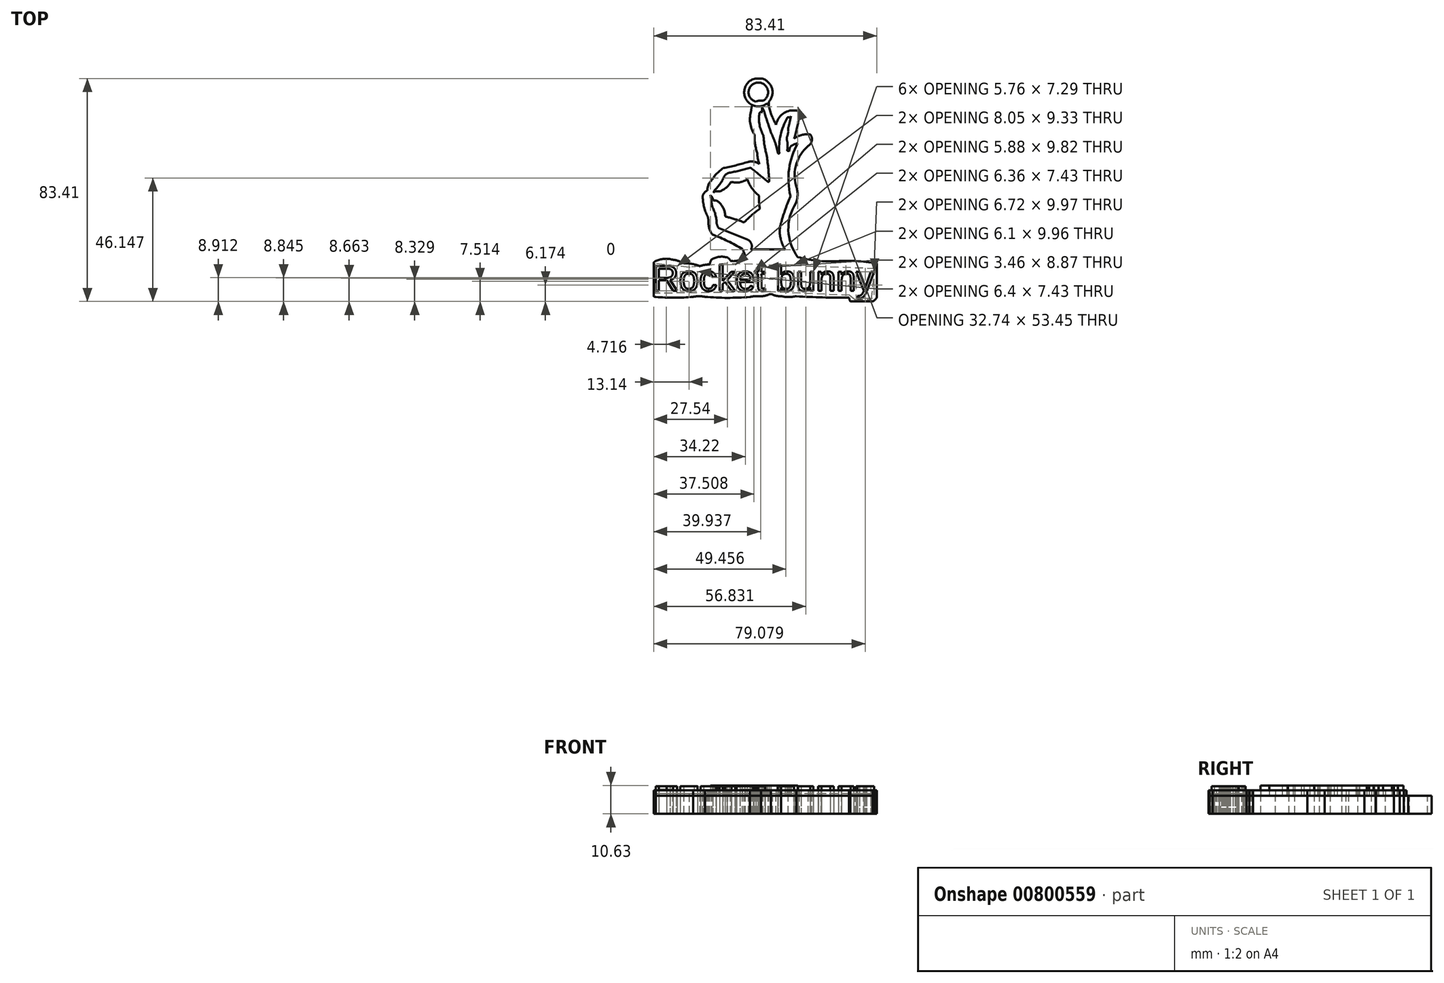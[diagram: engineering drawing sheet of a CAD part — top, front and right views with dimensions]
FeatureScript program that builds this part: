
annotation { "Feature Type Name" : "Feature", "Feature Type Description" : "" }
export const myFeature = defineFeature(function(context is Context, id is Id, definition is map)
    precondition{}
    {
        {
            var Q0;
            Q0=qCreatedBy(makeId("Top.planeOp"),FACE);
            var sketch = newSketch(context, id + "F0", { "sketchPlane" : qUnion([Q0])});
            skText(sketch, "E0", { "text": "Rocket bunny", "fontName": "Arimo-Regular.ttf"});
            skLineSegment(sketch, "E1.bottom", {"start": v(-48.47, 33.5) * mm, "end": v(34.94, 33.5) * mm});
            skLineSegment(sketch, "E1.top", {"start": v(-48.47, -49.92) * mm, "end": v(34.94, -49.92) * mm});
            skLineSegment(sketch, "E1.left", {"start": v(-48.47, 33.5) * mm, "end": v(-48.47, -49.92) * mm});
            skLineSegment(sketch, "E1.right", {"start": v(34.94, 33.5) * mm, "end": v(34.94, -49.92) * mm});
            const initialGuessF0  = {"E0": [-0.04889, -0.04592, 1, 0, 0.00976]};
            skSetInitialGuess(sketch, initialGuessF0);
            skSolve(sketch);
        }
        {
            var Q0;
            Q0=makeQuery(id+"F0.imprint","IMPRINT",FACE,{"disambiguationData":[TD([[makeQuery(id+"F0.imprint","IMPRINT",EDGE,{"derivedFrom":sQuery(id+"F0.wireOp",EDGE,"E0.sketch_text.stroke-0")}),-1.0]])]});
            var Q1;
            Q1=makeQuery(id+"F0.imprint","IMPRINT",FACE,{"disambiguationData":[TD([[makeQuery(id+"F0.imprint","IMPRINT",EDGE,{"derivedFrom":sQuery(id+"F0.wireOp",EDGE,"E0.sketch_text.stroke-19")}),-1.0]])]});
            var Q2;
            Q2=makeQuery(id+"F0.imprint","IMPRINT",FACE,{"disambiguationData":[TD([[makeQuery(id+"F0.imprint","IMPRINT",EDGE,{"derivedFrom":sQuery(id+"F0.wireOp",EDGE,"E0.sketch_text.stroke-34")}),-1.0]])]});
            var Q3;
            Q3=makeQuery(id+"F0.imprint","IMPRINT",FACE,{"disambiguationData":[TD([[makeQuery(id+"F0.imprint","IMPRINT",EDGE,{"derivedFrom":sQuery(id+"F0.wireOp",EDGE,"E0.sketch_text.stroke-52")}),-1.0]])]});
            var Q4;
            Q4=makeQuery(id+"F0.imprint","IMPRINT",FACE,{"disambiguationData":[TD([[makeQuery(id+"F0.imprint","IMPRINT",EDGE,{"derivedFrom":sQuery(id+"F0.wireOp",EDGE,"E0.sketch_text.stroke-64")}),-1.0]])]});
            var Q5;
            Q5=makeQuery(id+"F0.imprint","IMPRINT",FACE,{"disambiguationData":[TD([[makeQuery(id+"F0.imprint","IMPRINT",EDGE,{"derivedFrom":sQuery(id+"F0.wireOp",EDGE,"E0.sketch_text.stroke-82")}),-1.0]])]});
            var Q6;
            Q6=makeQuery(id+"F0.imprint","IMPRINT",FACE,{"disambiguationData":[TD([[makeQuery(id+"F0.imprint","IMPRINT",EDGE,{"derivedFrom":sQuery(id+"F0.wireOp",EDGE,"E0.sketch_text.stroke-99")}),-1.0]])]});
            var Q7;
            Q7=makeQuery(id+"F0.imprint","IMPRINT",FACE,{"disambiguationData":[TD([[makeQuery(id+"F0.imprint","IMPRINT",EDGE,{"derivedFrom":sQuery(id+"F0.wireOp",EDGE,"E0.sketch_text.stroke-124")}),-1.0]])]});
            var Q8;
            Q8=makeQuery(id+"F0.imprint","IMPRINT",FACE,{"disambiguationData":[TD([[makeQuery(id+"F0.imprint","IMPRINT",EDGE,{"derivedFrom":sQuery(id+"F0.wireOp",EDGE,"E0.sketch_text.stroke-145")}),-1.0]])]});
            var Q9;
            Q9=makeQuery(id+"F0.imprint","IMPRINT",FACE,{"disambiguationData":[TD([[makeQuery(id+"F0.imprint","IMPRINT",EDGE,{"derivedFrom":sQuery(id+"F0.wireOp",EDGE,"E0.sketch_text.stroke-166")}),-1.0]])]});
            var Q10;
            Q10=makeQuery(id+"F0.imprint","IMPRINT",FACE,{"disambiguationData":[TD([[makeQuery(id+"F0.imprint","IMPRINT",EDGE,{"derivedFrom":sQuery(id+"F0.wireOp",EDGE,"E0.sketch_text.stroke-187")}),-1.0]])]});
            extrude(context, id + "F1", {"entities" : qUnion([Q0, Q1, Q2, Q3, Q4, Q5, Q6, Q7, Q8, Q9, Q10]), "depth" : 25.4 * mm, "offsetDistance" : 25.4 * mm});
        }
        {
            var Q0;
            Q0 = qSketchRegion(id + "F0", true);
            extrude(context, id + "F2", {"entities" : qUnion([Q0]), "depth" : 21.84 * mm, "offsetDistance" : 25.4 * mm});
        }
        {
            var Q0;
            Q0=makeQuery(id+"F2.opExtrude","CAP_FACE",FACE,{"disambiguationData":[OSD([sQuery(id+"F0.wireOp",EDGE,"E0.sketch_text.stroke-0"),sQuery(id+"F0.wireOp",EDGE,"E0.sketch_text.stroke-1"),sQuery(id+"F0.wireOp",EDGE,"E0.sketch_text.stroke-2"),sQuery(id+"F0.wireOp",EDGE,"E0.sketch_text.stroke-3"),sQuery(id+"F0.wireOp",EDGE,"E0.sketch_text.stroke-4"),sQuery(id+"F0.wireOp",EDGE,"E0.sketch_text.stroke-5"),sQuery(id+"F0.wireOp",EDGE,"E0.sketch_text.stroke-6"),sQuery(id+"F0.wireOp",EDGE,"E0.sketch_text.stroke-7"),sQuery(id+"F0.wireOp",EDGE,"E0.sketch_text.stroke-8"),sQuery(id+"F0.wireOp",EDGE,"E0.sketch_text.stroke-9"),sQuery(id+"F0.wireOp",EDGE,"E0.sketch_text.stroke-10"),sQuery(id+"F0.wireOp",EDGE,"E0.sketch_text.stroke-11"),sQuery(id+"F0.wireOp",EDGE,"E0.sketch_text.stroke-19"),sQuery(id+"F0.wireOp",EDGE,"E0.sketch_text.stroke-20"),sQuery(id+"F0.wireOp",EDGE,"E0.sketch_text.stroke-21"),sQuery(id+"F0.wireOp",EDGE,"E0.sketch_text.stroke-22"),sQuery(id+"F0.wireOp",EDGE,"E0.sketch_text.stroke-23"),sQuery(id+"F0.wireOp",EDGE,"E0.sketch_text.stroke-24"),sQuery(id+"F0.wireOp",EDGE,"E0.sketch_text.stroke-25"),sQuery(id+"F0.wireOp",EDGE,"E0.sketch_text.stroke-34"),sQuery(id+"F0.wireOp",EDGE,"E0.sketch_text.stroke-35"),sQuery(id+"F0.wireOp",EDGE,"E0.sketch_text.stroke-36"),sQuery(id+"F0.wireOp",EDGE,"E0.sketch_text.stroke-37"),sQuery(id+"F0.wireOp",EDGE,"E0.sketch_text.stroke-38"),sQuery(id+"F0.wireOp",EDGE,"E0.sketch_text.stroke-39"),sQuery(id+"F0.wireOp",EDGE,"E0.sketch_text.stroke-40"),sQuery(id+"F0.wireOp",EDGE,"E0.sketch_text.stroke-41"),sQuery(id+"F0.wireOp",EDGE,"E0.sketch_text.stroke-42"),sQuery(id+"F0.wireOp",EDGE,"E0.sketch_text.stroke-43"),sQuery(id+"F0.wireOp",EDGE,"E0.sketch_text.stroke-44"),sQuery(id+"F0.wireOp",EDGE,"E0.sketch_text.stroke-45"),sQuery(id+"F0.wireOp",EDGE,"E0.sketch_text.stroke-46"),sQuery(id+"F0.wireOp",EDGE,"E0.sketch_text.stroke-47"),sQuery(id+"F0.wireOp",EDGE,"E0.sketch_text.stroke-48"),sQuery(id+"F0.wireOp",EDGE,"E0.sketch_text.stroke-49"),sQuery(id+"F0.wireOp",EDGE,"E0.sketch_text.stroke-50"),sQuery(id+"F0.wireOp",EDGE,"E0.sketch_text.stroke-51"),sQuery(id+"F0.wireOp",EDGE,"E0.sketch_text.stroke-52"),sQuery(id+"F0.wireOp",EDGE,"E0.sketch_text.stroke-53"),sQuery(id+"F0.wireOp",EDGE,"E0.sketch_text.stroke-54"),sQuery(id+"F0.wireOp",EDGE,"E0.sketch_text.stroke-55"),sQuery(id+"F0.wireOp",EDGE,"E0.sketch_text.stroke-56"),sQuery(id+"F0.wireOp",EDGE,"E0.sketch_text.stroke-57"),sQuery(id+"F0.wireOp",EDGE,"E0.sketch_text.stroke-58"),sQuery(id+"F0.wireOp",EDGE,"E0.sketch_text.stroke-59"),sQuery(id+"F0.wireOp",EDGE,"E0.sketch_text.stroke-60"),sQuery(id+"F0.wireOp",EDGE,"E0.sketch_text.stroke-61"),sQuery(id+"F0.wireOp",EDGE,"E0.sketch_text.stroke-62"),sQuery(id+"F0.wireOp",EDGE,"E0.sketch_text.stroke-63"),sQuery(id+"F0.wireOp",EDGE,"E0.sketch_text.stroke-64"),sQuery(id+"F0.wireOp",EDGE,"E0.sketch_text.stroke-65"),sQuery(id+"F0.wireOp",EDGE,"E0.sketch_text.stroke-66"),sQuery(id+"F0.wireOp",EDGE,"E0.sketch_text.stroke-67"),sQuery(id+"F0.wireOp",EDGE,"E0.sketch_text.stroke-68"),sQuery(id+"F0.wireOp",EDGE,"E0.sketch_text.stroke-69"),sQuery(id+"F0.wireOp",EDGE,"E0.sketch_text.stroke-70"),sQuery(id+"F0.wireOp",EDGE,"E0.sketch_text.stroke-71"),sQuery(id+"F0.wireOp",EDGE,"E0.sketch_text.stroke-72"),sQuery(id+"F0.wireOp",EDGE,"E0.sketch_text.stroke-73"),sQuery(id+"F0.wireOp",EDGE,"E0.sketch_text.stroke-74"),sQuery(id+"F0.wireOp",EDGE,"E0.sketch_text.stroke-75"),sQuery(id+"F0.wireOp",EDGE,"E0.sketch_text.stroke-76"),sQuery(id+"F0.wireOp",EDGE,"E0.sketch_text.stroke-82"),sQuery(id+"F0.wireOp",EDGE,"E0.sketch_text.stroke-83"),sQuery(id+"F0.wireOp",EDGE,"E0.sketch_text.stroke-84"),sQuery(id+"F0.wireOp",EDGE,"E0.sketch_text.stroke-85"),sQuery(id+"F0.wireOp",EDGE,"E0.sketch_text.stroke-86"),sQuery(id+"F0.wireOp",EDGE,"E0.sketch_text.stroke-87"),sQuery(id+"F0.wireOp",EDGE,"E0.sketch_text.stroke-88"),sQuery(id+"F0.wireOp",EDGE,"E0.sketch_text.stroke-89"),sQuery(id+"F0.wireOp",EDGE,"E0.sketch_text.stroke-90"),sQuery(id+"F0.wireOp",EDGE,"E0.sketch_text.stroke-91"),sQuery(id+"F0.wireOp",EDGE,"E0.sketch_text.stroke-92"),sQuery(id+"F0.wireOp",EDGE,"E0.sketch_text.stroke-93"),sQuery(id+"F0.wireOp",EDGE,"E0.sketch_text.stroke-94"),sQuery(id+"F0.wireOp",EDGE,"E0.sketch_text.stroke-95"),sQuery(id+"F0.wireOp",EDGE,"E0.sketch_text.stroke-96"),sQuery(id+"F0.wireOp",EDGE,"E0.sketch_text.stroke-97"),sQuery(id+"F0.wireOp",EDGE,"E0.sketch_text.stroke-98"),sQuery(id+"F0.wireOp",EDGE,"E0.sketch_text.stroke-99"),sQuery(id+"F0.wireOp",EDGE,"E0.sketch_text.stroke-100"),sQuery(id+"F0.wireOp",EDGE,"E0.sketch_text.stroke-101"),sQuery(id+"F0.wireOp",EDGE,"E0.sketch_text.stroke-102"),sQuery(id+"F0.wireOp",EDGE,"E0.sketch_text.stroke-103"),sQuery(id+"F0.wireOp",EDGE,"E0.sketch_text.stroke-104"),sQuery(id+"F0.wireOp",EDGE,"E0.sketch_text.stroke-105"),sQuery(id+"F0.wireOp",EDGE,"E0.sketch_text.stroke-106"),sQuery(id+"F0.wireOp",EDGE,"E0.sketch_text.stroke-107"),sQuery(id+"F0.wireOp",EDGE,"E0.sketch_text.stroke-108"),sQuery(id+"F0.wireOp",EDGE,"E0.sketch_text.stroke-109"),sQuery(id+"F0.wireOp",EDGE,"E0.sketch_text.stroke-110"),sQuery(id+"F0.wireOp",EDGE,"E0.sketch_text.stroke-111"),sQuery(id+"F0.wireOp",EDGE,"E0.sketch_text.stroke-112"),sQuery(id+"F0.wireOp",EDGE,"E0.sketch_text.stroke-113"),sQuery(id+"F0.wireOp",EDGE,"E0.sketch_text.stroke-114"),sQuery(id+"F0.wireOp",EDGE,"E0.sketch_text.stroke-115"),sQuery(id+"F0.wireOp",EDGE,"E0.sketch_text.stroke-124"),sQuery(id+"F0.wireOp",EDGE,"E0.sketch_text.stroke-125"),sQuery(id+"F0.wireOp",EDGE,"E0.sketch_text.stroke-126"),sQuery(id+"F0.wireOp",EDGE,"E0.sketch_text.stroke-127"),sQuery(id+"F0.wireOp",EDGE,"E0.sketch_text.stroke-128"),sQuery(id+"F0.wireOp",EDGE,"E0.sketch_text.stroke-129"),sQuery(id+"F0.wireOp",EDGE,"E0.sketch_text.stroke-130"),sQuery(id+"F0.wireOp",EDGE,"E0.sketch_text.stroke-131"),sQuery(id+"F0.wireOp",EDGE,"E0.sketch_text.stroke-132"),sQuery(id+"F0.wireOp",EDGE,"E0.sketch_text.stroke-133"),sQuery(id+"F0.wireOp",EDGE,"E0.sketch_text.stroke-134"),sQuery(id+"F0.wireOp",EDGE,"E0.sketch_text.stroke-135"),sQuery(id+"F0.wireOp",EDGE,"E0.sketch_text.stroke-136"),sQuery(id+"F0.wireOp",EDGE,"E0.sketch_text.stroke-137"),sQuery(id+"F0.wireOp",EDGE,"E0.sketch_text.stroke-138"),sQuery(id+"F0.wireOp",EDGE,"E0.sketch_text.stroke-139"),sQuery(id+"F0.wireOp",EDGE,"E0.sketch_text.stroke-140"),sQuery(id+"F0.wireOp",EDGE,"E0.sketch_text.stroke-141"),sQuery(id+"F0.wireOp",EDGE,"E0.sketch_text.stroke-142"),sQuery(id+"F0.wireOp",EDGE,"E0.sketch_text.stroke-143"),sQuery(id+"F0.wireOp",EDGE,"E0.sketch_text.stroke-144"),sQuery(id+"F0.wireOp",EDGE,"E0.sketch_text.stroke-145"),sQuery(id+"F0.wireOp",EDGE,"E0.sketch_text.stroke-146"),sQuery(id+"F0.wireOp",EDGE,"E0.sketch_text.stroke-147"),sQuery(id+"F0.wireOp",EDGE,"E0.sketch_text.stroke-148"),sQuery(id+"F0.wireOp",EDGE,"E0.sketch_text.stroke-149"),sQuery(id+"F0.wireOp",EDGE,"E0.sketch_text.stroke-150"),sQuery(id+"F0.wireOp",EDGE,"E0.sketch_text.stroke-151"),sQuery(id+"F0.wireOp",EDGE,"E0.sketch_text.stroke-152"),sQuery(id+"F0.wireOp",EDGE,"E0.sketch_text.stroke-153"),sQuery(id+"F0.wireOp",EDGE,"E0.sketch_text.stroke-154"),sQuery(id+"F0.wireOp",EDGE,"E0.sketch_text.stroke-155"),sQuery(id+"F0.wireOp",EDGE,"E0.sketch_text.stroke-156"),sQuery(id+"F0.wireOp",EDGE,"E0.sketch_text.stroke-157"),sQuery(id+"F0.wireOp",EDGE,"E0.sketch_text.stroke-158"),sQuery(id+"F0.wireOp",EDGE,"E0.sketch_text.stroke-159"),sQuery(id+"F0.wireOp",EDGE,"E0.sketch_text.stroke-160"),sQuery(id+"F0.wireOp",EDGE,"E0.sketch_text.stroke-161"),sQuery(id+"F0.wireOp",EDGE,"E0.sketch_text.stroke-162"),sQuery(id+"F0.wireOp",EDGE,"E0.sketch_text.stroke-163"),sQuery(id+"F0.wireOp",EDGE,"E0.sketch_text.stroke-164"),sQuery(id+"F0.wireOp",EDGE,"E0.sketch_text.stroke-165"),sQuery(id+"F0.wireOp",EDGE,"E0.sketch_text.stroke-166"),sQuery(id+"F0.wireOp",EDGE,"E0.sketch_text.stroke-167"),sQuery(id+"F0.wireOp",EDGE,"E0.sketch_text.stroke-168"),sQuery(id+"F0.wireOp",EDGE,"E0.sketch_text.stroke-169"),sQuery(id+"F0.wireOp",EDGE,"E0.sketch_text.stroke-170"),sQuery(id+"F0.wireOp",EDGE,"E0.sketch_text.stroke-171"),sQuery(id+"F0.wireOp",EDGE,"E0.sketch_text.stroke-172"),sQuery(id+"F0.wireOp",EDGE,"E0.sketch_text.stroke-173"),sQuery(id+"F0.wireOp",EDGE,"E0.sketch_text.stroke-174"),sQuery(id+"F0.wireOp",EDGE,"E0.sketch_text.stroke-175"),sQuery(id+"F0.wireOp",EDGE,"E0.sketch_text.stroke-176"),sQuery(id+"F0.wireOp",EDGE,"E0.sketch_text.stroke-177"),sQuery(id+"F0.wireOp",EDGE,"E0.sketch_text.stroke-178"),sQuery(id+"F0.wireOp",EDGE,"E0.sketch_text.stroke-179"),sQuery(id+"F0.wireOp",EDGE,"E0.sketch_text.stroke-180"),sQuery(id+"F0.wireOp",EDGE,"E0.sketch_text.stroke-181"),sQuery(id+"F0.wireOp",EDGE,"E0.sketch_text.stroke-182"),sQuery(id+"F0.wireOp",EDGE,"E0.sketch_text.stroke-183"),sQuery(id+"F0.wireOp",EDGE,"E0.sketch_text.stroke-184"),sQuery(id+"F0.wireOp",EDGE,"E0.sketch_text.stroke-185"),sQuery(id+"F0.wireOp",EDGE,"E0.sketch_text.stroke-186"),sQuery(id+"F0.wireOp",EDGE,"E0.sketch_text.stroke-187"),sQuery(id+"F0.wireOp",EDGE,"E0.sketch_text.stroke-188"),sQuery(id+"F0.wireOp",EDGE,"E0.sketch_text.stroke-189"),sQuery(id+"F0.wireOp",EDGE,"E0.sketch_text.stroke-190"),sQuery(id+"F0.wireOp",EDGE,"E0.sketch_text.stroke-191"),sQuery(id+"F0.wireOp",EDGE,"E0.sketch_text.stroke-192"),sQuery(id+"F0.wireOp",EDGE,"E0.sketch_text.stroke-193"),sQuery(id+"F0.wireOp",EDGE,"E0.sketch_text.stroke-194"),sQuery(id+"F0.wireOp",EDGE,"E0.sketch_text.stroke-195"),sQuery(id+"F0.wireOp",EDGE,"E0.sketch_text.stroke-196"),sQuery(id+"F0.wireOp",EDGE,"E0.sketch_text.stroke-197"),sQuery(id+"F0.wireOp",EDGE,"E0.sketch_text.stroke-198"),sQuery(id+"F0.wireOp",EDGE,"E0.sketch_text.stroke-199"),sQuery(id+"F0.wireOp",EDGE,"E0.sketch_text.stroke-200"),sQuery(id+"F0.wireOp",EDGE,"E0.sketch_text.stroke-201"),sQuery(id+"F0.wireOp",EDGE,"E0.sketch_text.stroke-202"),sQuery(id+"F0.wireOp",EDGE,"E0.sketch_text.stroke-203"),sQuery(id+"F0.wireOp",EDGE,"E0.sketch_text.stroke-204"),sQuery(id+"F0.wireOp",EDGE,"E1.bottom"),sQuery(id+"F0.wireOp",EDGE,"E1.top"),sQuery(id+"F0.wireOp",EDGE,"E1.left"),sQuery(id+"F0.wireOp",EDGE,"E1.right")])],"isStart":false});
            var sketch = newSketch(context, id + "F3", { "sketchPlane" : qUnion([Q0])});
            skArc(sketch, "E2", {"start": v(-12.1, -30.5) * mm, "mid": v(-11.93, -28.34) * mm, "end": v(-13.43, -26.79) * mm});
            skLineSegment(sketch, "E3", {"start": v(-13.43, -26.79) * mm, "end": v(-24.27, -22.44) * mm});
            skArc(sketch, "E4", {"start": v(-24.95, -20.72) * mm, "mid": v(-24.67, -21.6) * mm, "end": v(-24.27, -22.44) * mm});
            skArc(sketch, "E5", {"start": v(-24.95, -20.72) * mm, "mid": v(-25.43, -17.4) * mm, "end": v(-26.67, -14.28) * mm});
            skLineSegment(sketch, "E6", {"start": v(-26.67, -14.28) * mm, "end": v(-27.33, -10.13) * mm});
            skArc(sketch, "E7", {"start": v(-26.19, -12.12) * mm, "mid": v(-26.6, -11.03) * mm, "end": v(-27.33, -10.13) * mm});
            skArc(sketch, "E8", {"start": v(-24.2, -12.7) * mm, "mid": v(-25.13, -12.18) * mm, "end": v(-26.19, -12.12) * mm});
            skArc(sketch, "E9", {"start": v(-21.74, -17.71) * mm, "mid": v(-22.5, -14.97) * mm, "end": v(-24.2, -12.7) * mm});
            skArc(sketch, "E10", {"start": v(-21.74, -17.71) * mm, "mid": v(-21.61, -18.11) * mm, "end": v(-21.22, -18.27) * mm});
            skArc(sketch, "E11", {"start": v(-15.4, -20.08) * mm, "mid": v(-18.28, -19.08) * mm, "end": v(-21.22, -18.27) * mm});
            skArc(sketch, "E12", {"start": v(-15.4, -20.08) * mm, "mid": v(-14.9, -20.23) * mm, "end": v(-14.4, -20.08) * mm});
            skArc(sketch, "E13", {"start": v(-8.82, -15.25) * mm, "mid": v(-11.74, -17.52) * mm, "end": v(-14.4, -20.08) * mm});
            skArc(sketch, "E14", {"start": v(-9.13, -10.36) * mm, "mid": v(-9.05, -12.81) * mm, "end": v(-8.82, -15.25) * mm});
            skArc(sketch, "E15", {"start": v(-13.52, -4.19) * mm, "mid": v(-11.73, -7.56) * mm, "end": v(-9.13, -10.36) * mm});
            skArc(sketch, "E16", {"start": v(-19.57, -5.15) * mm, "mid": v(-16.43, -5.38) * mm, "end": v(-13.52, -4.19) * mm});
            skArc(sketch, "E17", {"start": v(-23.72, -8.68) * mm, "mid": v(-21.33, -7.28) * mm, "end": v(-19.57, -5.15) * mm});
            skArc(sketch, "E18", {"start": v(-25.31, -8.68) * mm, "mid": v(-24.51, -8.71) * mm, "end": v(-23.72, -8.68) * mm});
            skArc(sketch, "E19", {"start": v(-25.31, -8.68) * mm, "mid": v(-25.72, -8.86) * mm, "end": v(-26.01, -9.2) * mm});
            skArc(sketch, "E20", {"start": v(-25.72, -8.3) * mm, "mid": v(-25.94, -8.72) * mm, "end": v(-26.01, -9.2) * mm});
            skPoint(sketch, "E20.startSnap0", {"position": v(-25.72, -8.86) * mm});
            skArc(sketch, "E21", {"start": v(-25.72, -8.3) * mm, "mid": v(-23.57, -5.79) * mm, "end": v(-22, -2.9) * mm});
            skArc(sketch, "E22", {"start": v(-20.24, -1.76) * mm, "mid": v(-21.21, -2.18) * mm, "end": v(-22, -2.9) * mm});
            skArc(sketch, "E23", {"start": v(-20.24, -1.76) * mm, "mid": v(-16.4, -0.99) * mm, "end": v(-12.6, 0) * mm});
            skArc(sketch, "E24", {"start": v(-11.77, -0.28) * mm, "mid": v(-12.14, -0.02) * mm, "end": v(-12.6, 0) * mm});
            skArc(sketch, "E25", {"start": v(-5.88, -5.07) * mm, "mid": v(-8.8, -2.65) * mm, "end": v(-11.77, -0.28) * mm});
            skArc(sketch, "E26", {"start": v(-5.88, -5.07) * mm, "mid": v(-5.51, -5.18) * mm, "end": v(-5.28, -4.87) * mm});
            skArc(sketch, "E27", {"start": v(-5.28, -4.87) * mm, "mid": v(-5.66, 0.16) * mm, "end": v(-6.3, 5.17) * mm});
            skArc(sketch, "E28", {"start": v(-7.43, 12.13) * mm, "mid": v(-7.07, 8.62) * mm, "end": v(-6.3, 5.17) * mm});
            skArc(sketch, "E29", {"start": v(-8.93, 20.51) * mm, "mid": v(-8.91, 16.2) * mm, "end": v(-7.43, 12.13) * mm});
            skArc(sketch, "E30", {"start": v(-7.89, 20.87) * mm, "mid": v(-8.49, 20.92) * mm, "end": v(-8.93, 20.51) * mm});
            skArc(sketch, "E31", {"start": v(-8.02, 22.95) * mm, "mid": v(-7.98, 21.9) * mm, "end": v(-7.89, 20.87) * mm});
            skArc(sketch, "E32", {"start": v(-7.1, 20.87) * mm, "mid": v(-7.47, 21.95) * mm, "end": v(-8.02, 22.95) * mm});
            skArc(sketch, "E33", {"start": v(-7.1, 20.87) * mm, "mid": v(-5.9, 17.05) * mm, "end": v(-4.6, 13.25) * mm});
            skArc(sketch, "E34", {"start": v(-2, 5.54) * mm, "mid": v(-3.07, 9.48) * mm, "end": v(-4.6, 13.25) * mm});
            skArc(sketch, "E35", {"start": v(-2, 5.54) * mm, "mid": v(-1.76, 5.38) * mm, "end": v(-1.53, 5.54) * mm});
            skArc(sketch, "E36", {"start": v(1.43, 18.73) * mm, "mid": v(-1, 12.35) * mm, "end": v(-1.53, 5.54) * mm});
            skArc(sketch, "E37", {"start": v(2.4, 18.73) * mm, "mid": v(1.92, 19.02) * mm, "end": v(1.43, 18.73) * mm});
            skArc(sketch, "E38", {"start": v(2.4, 18.73) * mm, "mid": v(2.6, 19.04) * mm, "end": v(2.8, 19.36) * mm});
            skArc(sketch, "E39", {"start": v(2.65, 18.6) * mm, "mid": v(2.76, 18.97) * mm, "end": v(2.8, 19.36) * mm});
            skArc(sketch, "E40", {"start": v(1.89, 15.28) * mm, "mid": v(2.33, 16.92) * mm, "end": v(2.65, 18.6) * mm});
            skArc(sketch, "E41", {"start": v(1.89, 15.28) * mm, "mid": v(1.82, 14.48) * mm, "end": v(1.89, 13.69) * mm});
            skArc(sketch, "E42", {"start": v(1.43, 11.82) * mm, "mid": v(1.7, 12.75) * mm, "end": v(1.89, 13.69) * mm});
            skArc(sketch, "E43", {"start": v(1.43, 11.82) * mm, "mid": v(1.25, 10.95) * mm, "end": v(1.43, 10.07) * mm});
            skArc(sketch, "E44", {"start": v(1.43, 6.61) * mm, "mid": v(1.6, 8.34) * mm, "end": v(1.43, 10.07) * mm});
            skArc(sketch, "E45", {"start": v(1.43, 6.61) * mm, "mid": v(1.92, 6.38) * mm, "end": v(2.4, 6.61) * mm});
            skArc(sketch, "E46", {"start": v(3, 8.3) * mm, "mid": v(2.44, 7.55) * mm, "end": v(2.4, 6.61) * mm});
            skArc(sketch, "E47", {"start": v(5.4, 9.24) * mm, "mid": v(4.17, 8.88) * mm, "end": v(3, 8.3) * mm});
            skArc(sketch, "E48", {"start": v(5.4, 9.24) * mm, "mid": v(2.14, -0.37) * mm, "end": v(2.65, -10.5) * mm});
            skArc(sketch, "E49", {"start": v(2.65, -10.5) * mm, "mid": v(0.8, -15.31) * mm, "end": v(-0.78, -20.22) * mm});
            skArc(sketch, "E50", {"start": v(-0.78, -20.22) * mm, "mid": v(-1.34, -23.74) * mm, "end": v(-0.78, -27.26) * mm});
            skArc(sketch, "E51", {"start": v(-0.78, -27.26) * mm, "mid": v(-0.15, -28.92) * mm, "end": v(0.69, -30.48) * mm});
            skArc(sketch, "E52", {"start": v(0.69, -30.48) * mm, "mid": v(-5.7, -30.48) * mm, "end": v(-12.1, -30.5) * mm});
            skArc(sketch, "E53", {"start": v(4.78, -13.02) * mm, "mid": v(1.87, -23.26) * mm, "end": v(5.43, -33.29) * mm});
            skArc(sketch, "E54", {"start": v(-9.82, 5.89) * mm, "mid": v(-9.56, 3.66) * mm, "end": v(-9, 1.5) * mm});
            skArc(sketch, "E55", {"start": v(-10.8, 12.52) * mm, "mid": v(-10.6, 9.16) * mm, "end": v(-9.82, 5.89) * mm});
            skArc(sketch, "E56", {"start": v(-11.97, 21.54) * mm, "mid": v(-12.42, 16.9) * mm, "end": v(-10.8, 12.52) * mm});
            skArc(sketch, "E57", {"start": v(-5.4, 23.07) * mm, "mid": v(-9.35, 25.16) * mm, "end": v(-11.97, 21.54) * mm});
            skArc(sketch, "E58", {"start": v(-5.4, 23.07) * mm, "mid": v(-4.31, 19.52) * mm, "end": v(-2.71, 16.17) * mm});
            skArc(sketch, "E59", {"start": v(4.3, 21.54) * mm, "mid": v(-0.26, 20.23) * mm, "end": v(-2.71, 16.17) * mm});
            skArc(sketch, "E60", {"start": v(5.8, 19.36) * mm, "mid": v(5.72, 20.9) * mm, "end": v(4.3, 21.54) * mm});
            skArc(sketch, "E61", {"start": v(4, 10.96) * mm, "mid": v(5.15, 15.1) * mm, "end": v(5.8, 19.36) * mm});
            skArc(sketch, "E62", {"start": v(10.1, 12.52) * mm, "mid": v(6.89, 12.37) * mm, "end": v(4, 10.96) * mm});
            skArc(sketch, "E63", {"start": v(9.33, 8.3) * mm, "mid": v(10.66, 10.23) * mm, "end": v(10.1, 12.52) * mm});
            skArc(sketch, "E64", {"start": v(9.33, 8.3) * mm, "mid": v(4.86, 1.54) * mm, "end": v(4.73, -6.55) * mm});
            skArc(sketch, "E65", {"start": v(4.78, -13.02) * mm, "mid": v(5.32, -9.78) * mm, "end": v(4.73, -6.55) * mm});
            skArc(sketch, "E66", {"start": v(-9, 1.5) * mm, "mid": v(-11.07, 2.38) * mm, "end": v(-13.33, 2.24) * mm});
            skArc(sketch, "E67", {"start": v(-22.46, 0) * mm, "mid": v(-17.86, 1) * mm, "end": v(-13.33, 2.24) * mm});
            skArc(sketch, "E68", {"start": v(-22.46, 0) * mm, "mid": v(-24.8, -1.94) * mm, "end": v(-26.68, -4.34) * mm});
            skArc(sketch, "E69", {"start": v(-26.68, -4.34) * mm, "mid": v(-27.97, -6.21) * mm, "end": v(-28.46, -8.44) * mm});
            skArc(sketch, "E70", {"start": v(-28.46, -8.44) * mm, "mid": v(-29.5, -9.22) * mm, "end": v(-30.16, -10.34) * mm});
            skArc(sketch, "E71", {"start": v(-30.16, -10.34) * mm, "mid": v(-29.77, -14.08) * mm, "end": v(-28.57, -17.64) * mm});
            skArc(sketch, "E72", {"start": v(-28.03, -19.8) * mm, "mid": v(-28.16, -18.69) * mm, "end": v(-28.57, -17.64) * mm});
            skArc(sketch, "E73", {"start": v(-28.03, -19.8) * mm, "mid": v(-27.74, -22.45) * mm, "end": v(-26.57, -24.85) * mm});
            skArc(sketch, "E74", {"start": v(-15.29, -30.36) * mm, "mid": v(-20.8, -27.33) * mm, "end": v(-26.57, -24.85) * mm});
            skArc(sketch, "E75", {"start": v(-14.24, -33.5) * mm, "mid": v(-14.59, -31.88) * mm, "end": v(-15.29, -30.36) * mm});
            skArc(sketch, "E76", {"start": v(-19.74, -34.75) * mm, "mid": v(-16.88, -34.61) * mm, "end": v(-14.24, -33.5) * mm});
            skArc(sketch, "E77", {"start": v(-19.74, -34.75) * mm, "mid": v(-20.18, -34.03) * mm, "end": v(-20.86, -33.5) * mm});
            skArc(sketch, "E78", {"start": v(-20.86, -33.5) * mm, "mid": v(-23.99, -33.2) * mm, "end": v(-26.94, -34.29) * mm});
            skArc(sketch, "E79", {"start": v(-26.94, -34.29) * mm, "mid": v(-27.31, -35.14) * mm, "end": v(-27.57, -36.04) * mm});
            skArc(sketch, "E80", {"start": v(-27.57, -36.04) * mm, "mid": v(-29.45, -36.22) * mm, "end": v(-31.27, -36.74) * mm});
            skArc(sketch, "E81", {"start": v(-31.27, -36.74) * mm, "mid": v(-34.16, -35.84) * mm, "end": v(-37.18, -35.67) * mm});
            skArc(sketch, "E82", {"start": v(-37.18, -35.67) * mm, "mid": v(-39.2, -34.79) * mm, "end": v(-41.35, -34.29) * mm});
            skArc(sketch, "E83", {"start": v(-41.35, -34.29) * mm, "mid": v(-44.6, -33.96) * mm, "end": v(-47.76, -34.75) * mm});
            skArc(sketch, "E84", {"start": v(-47.76, -34.75) * mm, "mid": v(-48.95, -35.84) * mm, "end": v(-49.68, -37.3) * mm});
            skArc(sketch, "E85", {"start": v(-49.68, -46.46) * mm, "mid": v(-49.65, -41.88) * mm, "end": v(-49.68, -37.3) * mm});
            skArc(sketch, "E86", {"start": v(-49.68, -46.46) * mm, "mid": v(-49, -47.65) * mm, "end": v(-47.76, -48.23) * mm});
            skArc(sketch, "E87", {"start": v(-47.76, -48.23) * mm, "mid": v(-40.74, -48.48) * mm, "end": v(-33.72, -48.19) * mm});
            skArc(sketch, "E88", {"start": v(-29.31, -48.19) * mm, "mid": v(-31.52, -47.95) * mm, "end": v(-33.72, -48.19) * mm});
            skArc(sketch, "E89", {"start": v(-29.31, -48.19) * mm, "mid": v(-20.93, -48.54) * mm, "end": v(-12.54, -48.23) * mm});
            skArc(sketch, "E90", {"start": v(-8.4, -47.96) * mm, "mid": v(-10.48, -47.94) * mm, "end": v(-12.54, -48.23) * mm});
            skArc(sketch, "E91", {"start": v(-8.4, -47.96) * mm, "mid": v(-6.5, -47.7) * mm, "end": v(-4.73, -47.02) * mm});
            skArc(sketch, "E92", {"start": v(-4.73, -47.02) * mm, "mid": v(-2.84, -47.73) * mm, "end": v(-0.84, -47.96) * mm});
            skArc(sketch, "E93", {"start": v(-0.84, -47.96) * mm, "mid": v(1.98, -48.23) * mm, "end": v(4.8, -47.96) * mm});
            skArc(sketch, "E94", {"start": v(4.8, -47.96) * mm, "mid": v(14.68, -48.38) * mm, "end": v(24.56, -48.46) * mm});
            skArc(sketch, "E95", {"start": v(24.56, -48.46) * mm, "mid": v(25.03, -49.86) * mm, "end": v(25.9, -51.05) * mm});
            skArc(sketch, "E96", {"start": v(25.9, -51.05) * mm, "mid": v(30.14, -51.05) * mm, "end": v(34.1, -49.52) * mm});
            skArc(sketch, "E97", {"start": v(34.1, -49.52) * mm, "mid": v(37.02, -44.7) * mm, "end": v(38.27, -39.2) * mm});
            skArc(sketch, "E98", {"start": v(38.27, -39.2) * mm, "mid": v(37.83, -37.3) * mm, "end": v(36.4, -35.97) * mm});
            skArc(sketch, "E99", {"start": v(36.4, -35.97) * mm, "mid": v(27.7, -34.82) * mm, "end": v(18.92, -34.9) * mm});
            skArc(sketch, "E100", {"start": v(5.43, -33.29) * mm, "mid": v(12.1, -34.62) * mm, "end": v(18.92, -34.9) * mm});
            skLineSegment(sketch, "E101", {"start": v(-22.46, 0) * mm, "end": v(-48.47, 0) * mm});
            skLineSegment(sketch, "E102", {"start": v(-5.4, 23.07) * mm, "end": v(-5.49, 33.5) * mm});
            skLineSegment(sketch, "E103", {"start": v(4.73, -6.55) * mm, "end": v(34.94, -6.55) * mm});
            skPoint(sketch, "E103.endSnap0", {"position": v(34.94, -8.21) * mm});
            skLineSegment(sketch, "E104", {"start": v(-46.62, -37.52) * mm, "end": v(-46.62, -41.11) * mm});
            skLineSegment(sketch, "E105", {"start": v(-46.62, -41.11) * mm, "end": v(-42.7, -41.11) * mm});
            skLineSegment(sketch, "E106", {"start": v(-46.62, -37.52) * mm, "end": v(-42.8, -37.52) * mm});
            skArc(sketch, "E107", {"start": v(-42.7, -41.11) * mm, "mid": v(-41.01, -39.27) * mm, "end": v(-42.8, -37.52) * mm});
            skEllipse(sketch, "E108", {"center": v(-35.34, -42.22) * mm, "majorRadius": 3.36 * mm, "minorRadius": 2.29 * mm, "majorAxis": v(0.05, -1)});
            skArc(sketch, "E109", {"start": v(-11.78, -41.85) * mm, "mid": v(-14.15, -39.13) * mm, "end": v(-16.6, -41.78) * mm});
            skLineSegment(sketch, "E110", {"start": v(-16.6, -41.78) * mm, "end": v(-11.78, -41.85) * mm});
            skEllipse(sketch, "E111", {"center": v(1.1, -42.34) * mm, "majorRadius": 3.25 * mm, "minorRadius": 2.35 * mm, "majorAxis": v(0, -1)});
            skCircle(sketch, "E112", {"center": v(-9.35, 28.33) * mm, "radius": 5.3 * mm});
            skPoint(sketch, "E112.centerSnap0", {"position": v(-9.35, 25.16) * mm});
            skCircle(sketch, "E113", {"center": v(-9.35, 28.33) * mm, "radius": 3.65 * mm});
            skSolve(sketch);
        }
        {
            var Q0;
            Q0=makeQuery(id+"F3.imprint","IMPRINT",FACE,{"disambiguationData":[TD([[makeQuery(id+"F3.imprint","IMPRINT",EDGE,{"derivedFrom":sQuery(id+"F3.wireOp",EDGE,"E2")}),-1.0]])]});
            extrude(context, id + "F4", {"entities" : qUnion([Q0]), "operationType" : NewBodyOperationType.ADD, "depth" : 3.8 * mm, "offsetDistance" : 25.4 * mm});
        }
        {
            var Q0;
            Q0=makeQuery(id+"F3.imprint","IMPRINT",FACE,{"disambiguationData":[TD([[makeQuery(id+"F3.imprint","IMPRINT",EDGE,{"derivedFrom":sQuery(id+"F3.wireOp",EDGE,"E2")}),1.0]])]});
            extrude(context, id + "F5", {"entities" : qUnion([Q0]), "depth" : 2.03 * mm, "offsetDistance" : 25.4 * mm});
        }
        {
            var Q0;
            Q0=makeQuery(id+"F3.imprint","IMPRINT",FACE,{"disambiguationData":[TD([[makeQuery(id+"F3.imprint","IMPRINT",EDGE,{"derivedFrom":sQuery(id+"F3.wireOp",EDGE,"E54")}),-1.0]])]});
            extrude(context, id + "F6", {"entities" : qUnion([Q0]), "operationType" : NewBodyOperationType.REMOVE, "oppositeDirection" : true, "depth" : 25.4 * mm, "offsetDistance" : 25.4 * mm});
        }
        {
            var Q0;
            Q0=makeQuery(id+"F3.imprint","IMPRINT",FACE,{"disambiguationData":[TD([[makeQuery(id+"F3.imprint","IMPRINT",EDGE,{"derivedFrom":sQuery(id+"F3.wireOp",EDGE,"E58")}),1.0]])]});
            extrude(context, id + "F7", {"entities" : qUnion([Q0]), "operationType" : NewBodyOperationType.REMOVE, "oppositeDirection" : true, "depth" : 25.4 * mm, "offsetDistance" : 25.4 * mm});
        }
        {
            var Q0;
            Q0=makeQuery(id+"F3.imprint","IMPRINT",FACE,{"disambiguationData":[TD([[makeQuery(id+"F3.imprint","IMPRINT",EDGE,{"derivedFrom":sQuery(id+"F3.wireOp",EDGE,"E53")}),1.0]])]});
            extrude(context, id + "F8", {"entities" : qUnion([Q0]), "operationType" : NewBodyOperationType.REMOVE, "oppositeDirection" : true, "depth" : 25.4 * mm, "offsetDistance" : 25.4 * mm});
        }
        {
            var Q0;
            Q0=makeQuery(id+"F3.imprint","IMPRINT",FACE,{"disambiguationData":[TD([[makeQuery(id+"F3.imprint","IMPRINT",EDGE,{"derivedFrom":sQuery(id+"F3.wireOp",EDGE,"E68")}),-1.0]])]});
            extrude(context, id + "F9", {"entities" : qUnion([Q0]), "operationType" : NewBodyOperationType.REMOVE, "oppositeDirection" : true, "depth" : 25.4 * mm, "offsetDistance" : 25.4 * mm});
        }
        {
            var Q0;
            {var subQ4=sQuery(id+"F3.wireOp",EDGE,"E87");Q0=makeQuery(id+"F3.imprint","IMPRINT",FACE,{"disambiguationData":[TD([[makeQuery(id+"F3.imprint","IMPRINT",EDGE,{"derivedFrom":subQ4}),-1.0]])]});}
            extrude(context, id + "F10", {"entities" : qUnion([Q0]), "operationType" : NewBodyOperationType.REMOVE, "oppositeDirection" : true, "depth" : 25.4 * mm, "offsetDistance" : 25.4 * mm});
        }
        {
            var Q0;
            {var subQ0=sQuery(id+"F3.wireOp",EDGE,"E97");var subQ1=sQuery(id+"F3.wireOp",EDGE,"E96");var subQ2=makeQuery(id+"F3.imprint","INTERSECT",VERTEX,{"derivedFrom":[subQ1,subQ0]});Q0=makeQuery(id+"F3.imprint","IMPRINT",FACE,{"disambiguationData":[TD([[makeQuery(id+"F3.imprint","IMPRINT",EDGE,{"disambiguationData":[TD([[subQ2,1.0]])],"derivedFrom":subQ1}),-1.0]])]});}
            extrude(context, id + "F11", {"entities" : qUnion([Q0]), "operationType" : NewBodyOperationType.REMOVE, "oppositeDirection" : true, "depth" : 25.4 * mm, "offsetDistance" : 25.4 * mm});
        }
        {
            var Q0;
            Q0=makeQuery(id+"F3.imprint","IMPRINT",FACE,{"disambiguationData":[TD([[makeQuery(id+"F3.imprint","IMPRINT",EDGE,{"derivedFrom":sQuery(id+"F3.wireOp",EDGE,"E104")}),1.0]])]});
            extrude(context, id + "F12", {"entities" : qUnion([Q0]), "operationType" : NewBodyOperationType.ADD, "oppositeDirection" : true, "depth" : 21.83 * mm, "offsetDistance" : 25.4 * mm, "hasSecondDirection" : true, "secondDirectionOppositeDirection" : false, "secondDirectionDepth" : 2.4 * mm});
        }
        {
            var Q0;
            Q0=makeQuery(id+"F3.imprint","IMPRINT",FACE,{"disambiguationData":[TD([[makeQuery(id+"F3.imprint","IMPRINT",EDGE,{"derivedFrom":sQuery(id+"F3.wireOp",EDGE,"E108")}),1.0]])]});
            extrude(context, id + "F13", {"entities" : qUnion([Q0]), "operationType" : NewBodyOperationType.ADD, "depth" : 2.06 * mm, "offsetDistance" : 25.4 * mm, "hasSecondDirection" : true, "secondDirectionOppositeDirection" : true, "secondDirectionDepth" : 21.82 * mm});
        }
        {
            var Q0;
            Q0=makeQuery(id+"F3.imprint","IMPRINT",FACE,{"disambiguationData":[TD([[makeQuery(id+"F3.imprint","IMPRINT",EDGE,{"derivedFrom":sQuery(id+"F3.wireOp",EDGE,"E109")}),1.0]])]});
            extrude(context, id + "F14", {"entities" : qUnion([Q0]), "operationType" : NewBodyOperationType.ADD, "depth" : 2.41 * mm, "offsetDistance" : 25.4 * mm, "hasSecondDirection" : true, "secondDirectionOppositeDirection" : true, "secondDirectionDepth" : 21.82 * mm});
        }
        {
            var Q0;
            Q0=makeQuery(id+"F3.imprint","IMPRINT",FACE,{"disambiguationData":[TD([[makeQuery(id+"F3.imprint","IMPRINT",EDGE,{"derivedFrom":sQuery(id+"F3.wireOp",EDGE,"E111")}),1.0]])]});
            extrude(context, id + "F15", {"entities" : qUnion([Q0]), "operationType" : NewBodyOperationType.ADD, "depth" : 2 * mm, "offsetDistance" : 25 * mm, "hasSecondDirection" : true, "secondDirectionOppositeDirection" : true, "secondDirectionDepth" : 21.84 * mm});
        }
        {
            var Q0;
            {var subQ0=sQuery(id+"F3.wireOp",EDGE,"E102");var subQ1=makeQuery(id+"F2.opExtrude","CAP_EDGE",EDGE,{"disambiguationData":[OSD([sQuery(id+"F0.wireOp",EDGE,"E1.bottom")])],"isStart":false});var subQ2=makeQuery(id+"F3.imprint","INTERSECT",VERTEX,{"derivedFrom":[subQ1,subQ0]});Q0=makeQuery(id+"F3.imprint","IMPRINT",FACE,{"disambiguationData":[TD([[makeQuery(id+"F3.imprint","IMPRINT",EDGE,{"disambiguationData":[TD([[subQ2,1.0]])],"derivedFrom":subQ0}),1.0]])]});}
            extrude(context, id + "F16", {"entities" : qUnion([Q0]), "operationType" : NewBodyOperationType.REMOVE, "oppositeDirection" : true, "depth" : 25 * mm, "offsetDistance" : 25 * mm});
        }
        {
            var Q0;
            {var subQ0=sQuery(id+"F3.wireOp",EDGE,"E113");var subQ1=sQuery(id+"F3.wireOp",EDGE,"E57");var subQ2=makeQuery(id+"F3.imprint","INTERSECT",VERTEX,{"disambiguationData":[OD(0.0)],"derivedFrom":[subQ1,subQ0]});Q0=makeQuery(id+"F3.imprint","IMPRINT",FACE,{"disambiguationData":[TD([[makeQuery(id+"F3.imprint","IMPRINT",EDGE,{"disambiguationData":[TD([[subQ2,-1.0]])],"derivedFrom":subQ1}),-1.0]])]});}
            extrude(context, id + "F17", {"entities" : qUnion([Q0]), "operationType" : NewBodyOperationType.REMOVE, "oppositeDirection" : true, "depth" : 25 * mm, "offsetDistance" : 25 * mm});
        }
        {
            var Q0;
            Q0=qCreatedBy(makeId("Right.planeOp"),FACE);
            var sketch = newSketch(context, id + "F18", { "sketchPlane" : qUnion([Q0])});
            skLineSegment(sketch, "E114.bottom", {"start": v(42.19, 15.03) * mm, "end": v(-64.5, 15.03) * mm});
            skLineSegment(sketch, "E114.top", {"start": v(42.19, -2.04) * mm, "end": v(-64.5, -2.04) * mm});
            skLineSegment(sketch, "E114.left", {"start": v(42.19, 15.03) * mm, "end": v(42.19, -2.04) * mm});
            skLineSegment(sketch, "E114.right", {"start": v(-64.5, 15.03) * mm, "end": v(-64.5, -2.04) * mm});
            skSolve(sketch);
        }
        {
            var Q0;
            Q0=makeQuery(id+"F18.imprint","IMPRINT",FACE,{"disambiguationData":[TD([[makeQuery(id+"F18.imprint","IMPRINT",EDGE,{"derivedFrom":sQuery(id+"F18.wireOp",EDGE,"E114.bottom")}),1.0]])]});
            extrude(context, id + "F19", {"entities" : qUnion([Q0]), "operationType" : NewBodyOperationType.REMOVE, "depth" : 51.7 * mm, "offsetDistance" : 25 * mm, "hasSecondDirection" : true, "secondDirectionOppositeDirection" : true, "secondDirectionDepth" : 64.5 * mm});
        }
        {
            var Q0;
            Q0=makeQuery(id+"F19.boolean.opBoolean","COPY",FACE,{"disambiguationData":[TD([makeQuery(id+"F2.opExtrude","SWEPT_FACE",FACE,{"disambiguationData":[OSD([sQuery(id+"F0.wireOp",EDGE,"E0.sketch_text.stroke-0")])]})])],"derivedFrom":makeQuery(id+"F19.opExtrude","SWEPT_FACE",FACE,{"disambiguationData":[OSD([sQuery(id+"F18.wireOp",EDGE,"E114.bottom")])]})});
            var sketch = newSketch(context, id + "F20", { "sketchPlane" : qUnion([Q0])});
            skPoint(sketch, "E115.endSnap0", {"position": v(24.75, 49.2) * mm});
            skLineSegment(sketch, "E116", {"start": v(24.75, 47.62) * mm, "end": v(26.7, 49.06) * mm});
            skLineSegment(sketch, "E117", {"start": v(26.7, 49.06) * mm, "end": v(32.88, 49.06) * mm});
            skLineSegment(sketch, "E118", {"start": v(32.88, 49.06) * mm, "end": v(34.4, 37.62) * mm});
            skLineSegment(sketch, "E119", {"start": v(34.4, 37.62) * mm, "end": v(-21.14, 35.7) * mm});
            skLineSegment(sketch, "E120", {"start": v(-21.14, 35.7) * mm, "end": v(-35.32, 37.15) * mm});
            skLineSegment(sketch, "E121", {"start": v(-35.32, 37.15) * mm, "end": v(-48.14, 35.7) * mm});
            skLineSegment(sketch, "E122", {"start": v(-48.14, 35.7) * mm, "end": v(-48.14, 46.83) * mm});
            skLineSegment(sketch, "E123", {"start": v(24.75, 47.62) * mm, "end": v(-4.73, 46.32) * mm});
            skLineSegment(sketch, "E124", {"start": v(-4.73, 46.32) * mm, "end": v(-48.14, 46.83) * mm});
            skSolve(sketch);
        }
        {
            var Q0;
            Q0 = qSketchRegion(id + "F20", true);
            extrude(context, id + "F21", {"entities" : qUnion([Q0]), "oppositeDirection" : true, "depth" : 7.5 * mm, "offsetDistance" : 25 * mm, "hasSecondDirection" : true, "secondDirectionOppositeDirection" : false, "secondDirectionDepth" : 0.01 * mm});
        }
    });
